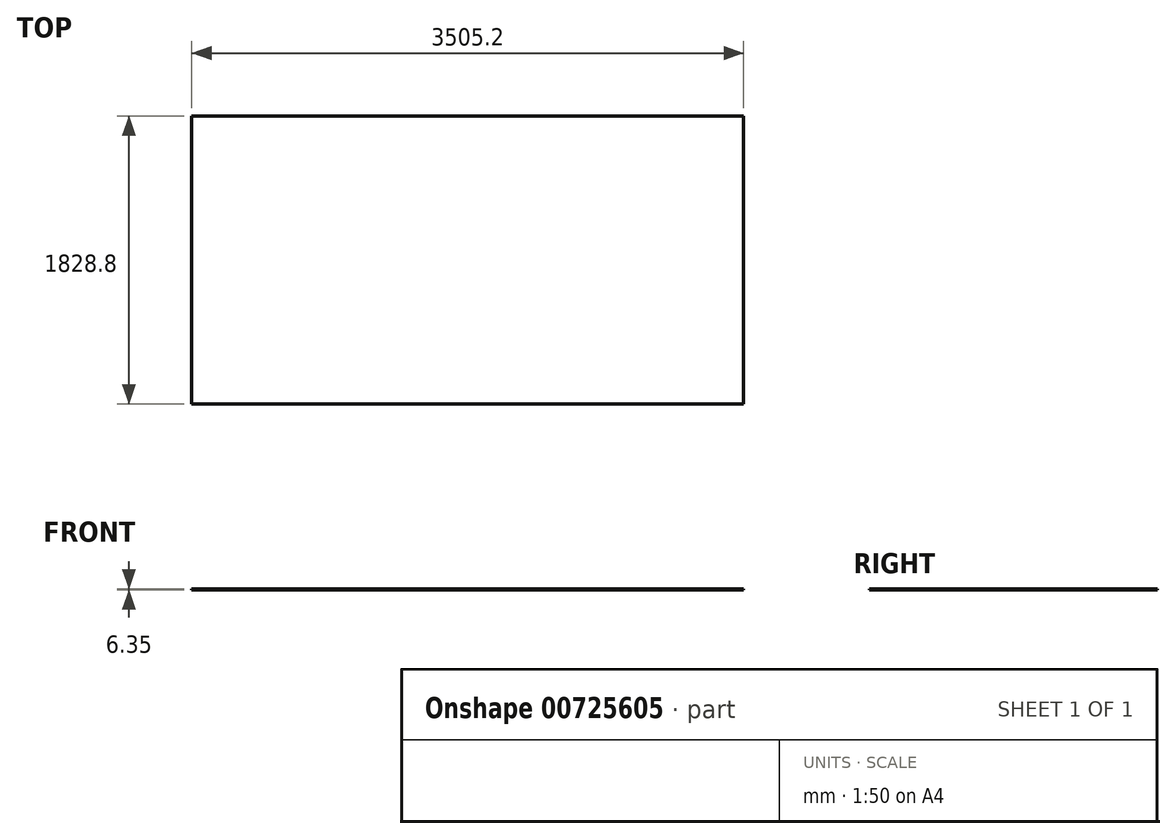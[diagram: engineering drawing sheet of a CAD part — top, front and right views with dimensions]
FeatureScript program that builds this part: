
annotation { "Feature Type Name" : "Feature", "Feature Type Description" : "" }
export const myFeature = defineFeature(function(context is Context, id is Id, definition is map)
    precondition{}
    {
        {
            var Q0;
            Q0=qCreatedBy(makeId("Top.planeOp"),FACE);
            var sketch = newSketch(context, id + "F0", { "sketchPlane" : qUnion([Q0])});
            skLineSegment(sketch, "E0.bottom", {"start": v(-1752.6, -914.4) * mm, "end": v(1752.6, -914.4) * mm});
            skLineSegment(sketch, "E0.top", {"start": v(-1752.6, 914.4) * mm, "end": v(1752.6, 914.4) * mm});
            skLineSegment(sketch, "E0.left", {"start": v(-1752.6, -914.4) * mm, "end": v(-1752.6, 914.4) * mm});
            skLineSegment(sketch, "E0.right", {"start": v(1752.6, -914.4) * mm, "end": v(1752.6, 914.4) * mm});
            skPoint(sketch, "E0.middle", {"position": v(0, 0) * mm});
            skSolve(sketch);
        }
        {
            var Q0;
            Q0 = qSketchRegion(id + "F0", true);
            extrude(context, id + "F1", {"entities" : qUnion([Q0]), "depth" : 6.35 * mm, "offsetDistance" : 25.4 * mm});
        }
    });
